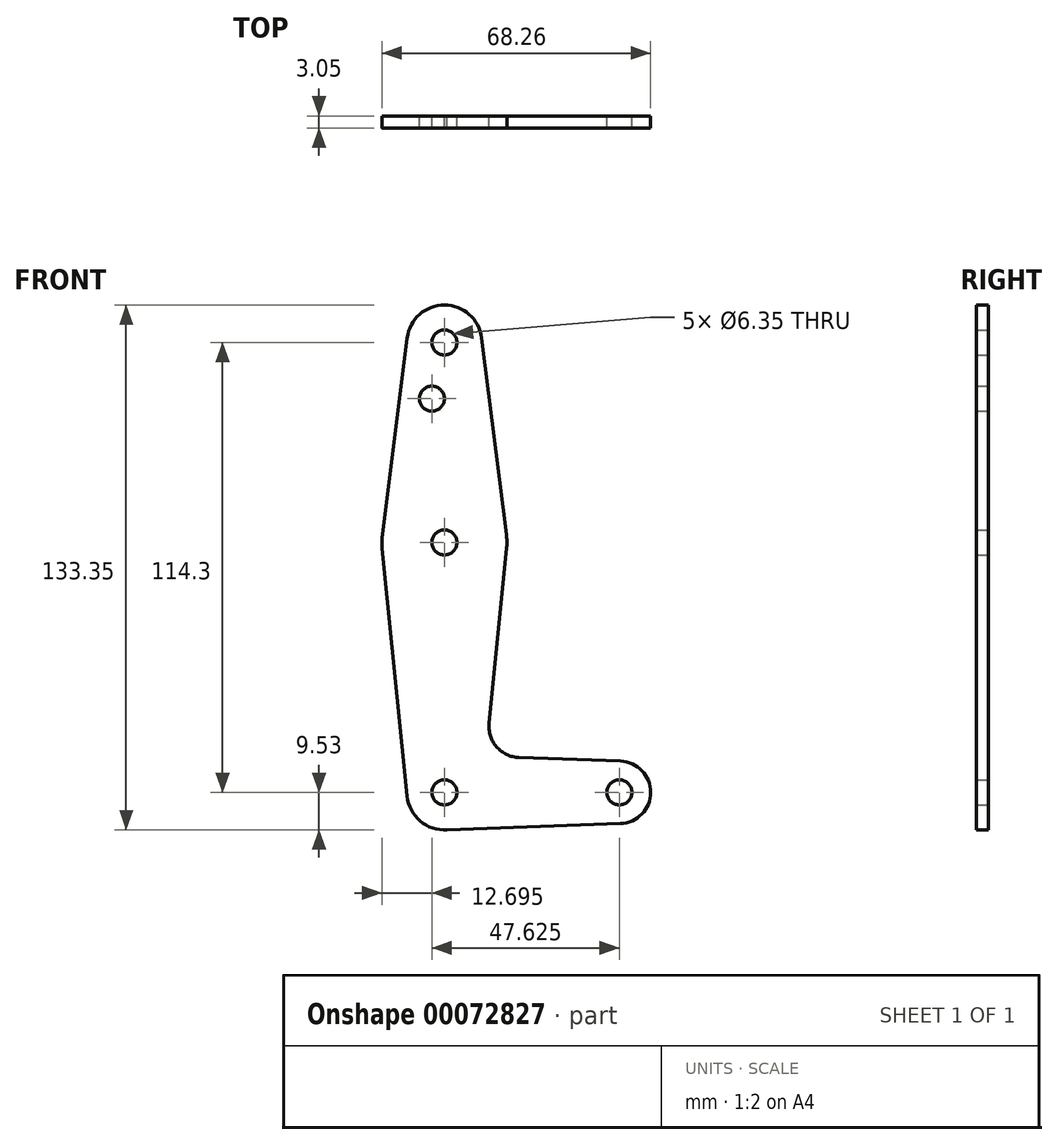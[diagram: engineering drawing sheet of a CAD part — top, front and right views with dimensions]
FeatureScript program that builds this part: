
annotation { "Feature Type Name" : "Feature", "Feature Type Description" : "" }
export const myFeature = defineFeature(function(context is Context, id is Id, definition is map)
    precondition{}
    {
        {
            var Q0;
            Q0=qCreatedBy(makeId("Front.planeOp"),FACE);
            var sketch = newSketch(context, id + "F0", { "sketchPlane" : qUnion([Q0])});
            skCircle(sketch, "E0", {"center": v(0, 0) * mm, "radius": 15.88 * mm});
            skCircle(sketch, "E1", {"center": v(0, 50.8) * mm, "radius": 9.53 * mm});
            skCircle(sketch, "E2", {"center": v(0, -63.5) * mm, "radius": 9.53 * mm});
            skLineSegment(sketch, "E3", {"start": v(0, 50.8) * mm, "end": v(0, 0) * mm, "construction": true});
            skLineSegment(sketch, "E4", {"start": v(0, 0) * mm, "end": v(0, -63.5) * mm, "construction": true});
            skCircle(sketch, "E5", {"center": v(44.45, -63.5) * mm, "radius": 7.94 * mm});
            skLineSegment(sketch, "E6", {"start": v(0, -63.5) * mm, "end": v(44.45, -63.5) * mm, "construction": true});
            skLineSegment(sketch, "E7", {"start": v(-9.45, 52) * mm, "end": v(-15.75, 1.98) * mm});
            skLineSegment(sketch, "E8", {"start": v(9.45, 52) * mm, "end": v(15.75, 1.98) * mm});
            skLineSegment(sketch, "E9", {"start": v(-15.8, -1.59) * mm, "end": v(-9.48, -64.45) * mm});
            skLineSegment(sketch, "E10", {"start": v(11.34, -45.91) * mm, "end": v(15.8, -1.59) * mm});
            skLineSegment(sketch, "E11", {"start": v(18.97, -54.65) * mm, "end": v(44.73, -55.57) * mm});
            skLineSegment(sketch, "E12", {"start": v(0, -73.03) * mm, "end": v(44.73, -71.43) * mm});
            skCircle(sketch, "E13", {"center": v(-3.17, 36.53) * mm, "radius": 3.18 * mm});
            skCircle(sketch, "E14", {"center": v(0, 50.8) * mm, "radius": 3.18 * mm});
            skCircle(sketch, "E15", {"center": v(0, 0) * mm, "radius": 3.18 * mm});
            skCircle(sketch, "E16", {"center": v(0, -63.5) * mm, "radius": 3.18 * mm});
            skCircle(sketch, "E17", {"center": v(44.45, -63.5) * mm, "radius": 3.18 * mm});
            skPoint(sketch, "E18.newPointB", {"position": v(0, -53.97) * mm});
            skArc(sketch, "E18.filletArc", {"start": v(11.34, -45.91) * mm, "mid": v(13.26, -51.93) * mm, "end": v(18.97, -54.65) * mm});
            skSolve(sketch);
        }
        {
            var Q0;
            Q0 = qSketchRegion(id + "F0", true);
            extrude(context, id + "F1", {"entities" : qUnion([Q0]), "depth" : 3.05 * mm});
        }
    });
